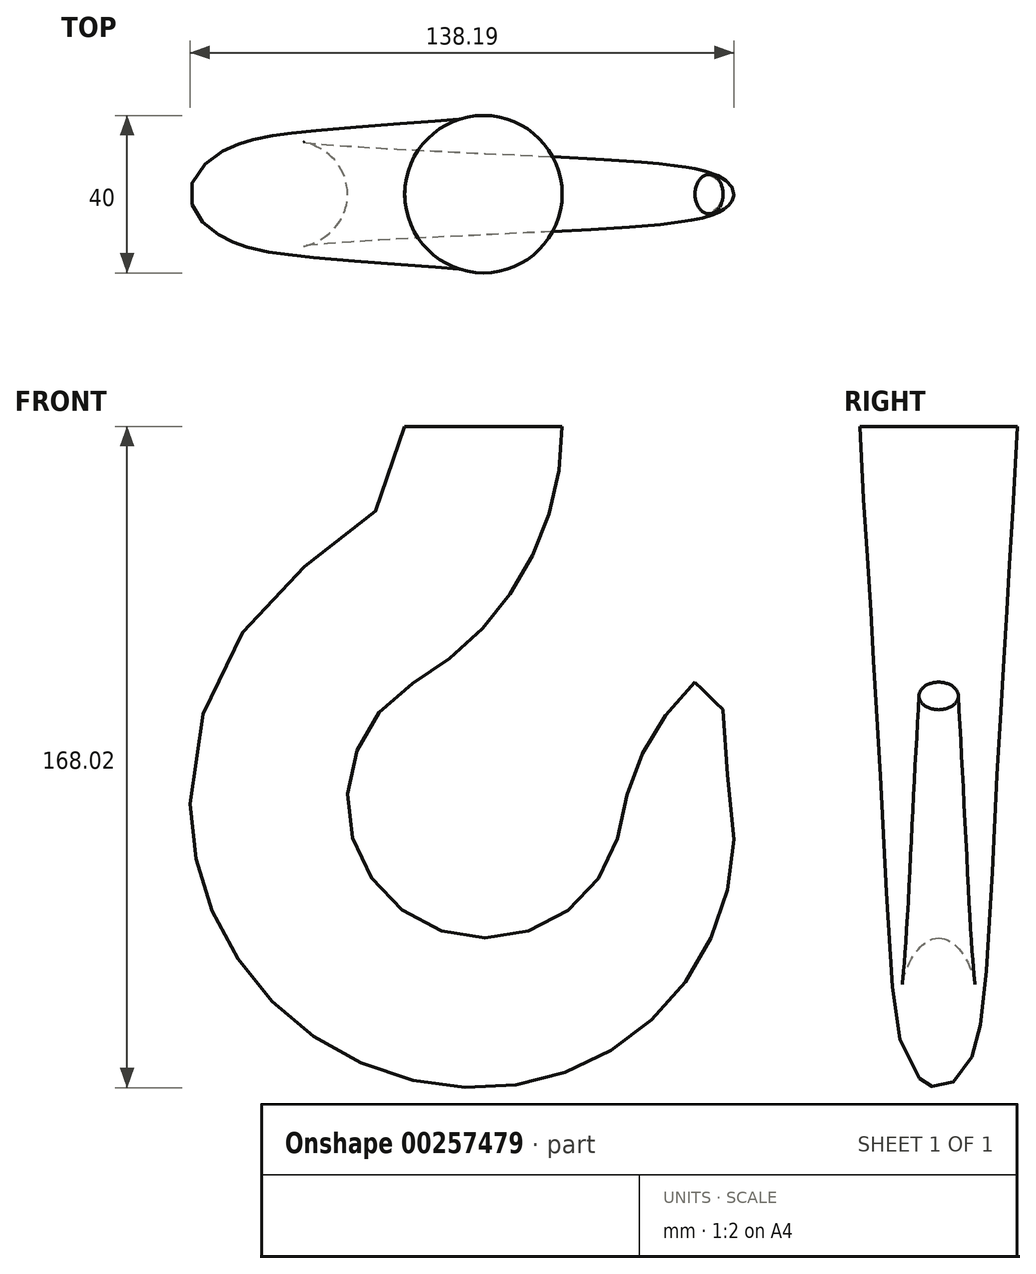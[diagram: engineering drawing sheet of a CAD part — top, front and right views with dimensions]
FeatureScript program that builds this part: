
annotation { "Feature Type Name" : "Feature", "Feature Type Description" : "" }
export const myFeature = defineFeature(function(context is Context, id is Id, definition is map)
    precondition{}
    {
        {
            var Q0;
            Q0=qCreatedBy(makeId("Front.planeOp"),FACE);
            var sketch = newSketch(context, id + "F0", { "sketchPlane" : qUnion([Q0])});
            skLineSegment(sketch, "E0", {"start": v(-20, 0) * mm, "end": v(20, 0) * mm, "construction": true});
            skArc(sketch, "E1", {"start": v(-37.36, -30.23) * mm, "mid": v(-24.65, -17.43) * mm, "end": v(-20, 0) * mm});
            skArc(sketch, "E2", {"start": v(-17.2, -64.77) * mm, "mid": v(10.04, -37.35) * mm, "end": v(20, 0) * mm});
            skLineSegment(sketch, "E3", {"start": v(-112.46, -95) * mm, "end": v(91.55, -95) * mm, "construction": true});
            skArc(sketch, "E4", {"start": v(-37.36, -30.23) * mm, "mid": v(-64.59, -57.65) * mm, "end": v(-74.55, -95) * mm});
            skArc(sketch, "E5", {"start": v(-74.55, -95) * mm, "mid": v(-52.62, -147.17) * mm, "end": v(0, -168) * mm});
            skArc(sketch, "E6", {"start": v(53.73, -65) * mm, "mid": v(41.39, -81) * mm, "end": v(35.06, -100.2) * mm});
            skLineSegment(sketch, "E7", {"start": v(53.73, -65) * mm, "end": v(60.87, -72) * mm, "construction": true});
            skArc(sketch, "E8", {"start": v(60.87, -72) * mm, "mid": v(60.74, -80.17) * mm, "end": v(61.94, -88.24) * mm});
            skCircle(sketch, "E9", {"center": v(57.3, -68.5) * mm, "radius": 5 * mm, "construction": true});
            skArc(sketch, "E10", {"start": v(0, -168) * mm, "mid": v(49.97, -142.88) * mm, "end": v(61.94, -88.24) * mm});
            skArc(sketch, "E11", {"start": v(-17.2, -64.77) * mm, "mid": v(-19.19, -123.97) * mm, "end": v(35.06, -100.2) * mm});
            skSolve(sketch);
        }
        {
            var Q0;
            Q0=qCreatedBy(makeId("Top.planeOp"),FACE);
            var sketch = newSketch(context, id + "F1", { "sketchPlane" : qUnion([Q0])});
            skLineSegment(sketch, "E12.0", {"start": v(-20, 0) * mm, "end": v(20, 0) * mm, "construction": true});
            skCircle(sketch, "E13", {"center": v(0, 0) * mm, "radius": 20 * mm});
            skSolve(sketch);
        }
        {
            var Q0;
            Q0=sQuery(id+"F0.wireOp",EDGE,"E7");
            cPlane(context, id + "F2", {"entities" : qUnion([Q0]), "cplaneType" : CPlaneType.LINE_ANGLE, "offset" : 25 * mm, "angle" : 90 * degree, "width" : 150 * mm, "height" : 150 * mm});
        }
        {
            var Q0;
            Q0=qCreatedBy(id+"F2.planeOp",FACE);
            var sketch = newSketch(context, id + "F3", { "sketchPlane" : qUnion([Q0])});
            skLineSegment(sketch, "E14.0", {"start": v(83.87, 0) * mm, "end": v(93.87, 0) * mm, "construction": true});
            skCircle(sketch, "E15", {"center": v(88.87, 0) * mm, "radius": 5 * mm});
            skSolve(sketch);
        }
        {
            var Q0;
            Q0=qCreatedBy(makeId("Front.planeOp"),FACE);
            var sketch = newSketch(context, id + "F4", { "sketchPlane" : qUnion([Q0])});
            skArc(sketch, "E16.0", {"start": v(-37.36, -30.23) * mm, "mid": v(-24.65, -17.43) * mm, "end": v(-20, 0) * mm});
            skArc(sketch, "E17.0", {"start": v(-37.36, -30.23) * mm, "mid": v(-64.59, -57.65) * mm, "end": v(-74.55, -95) * mm});
            skArc(sketch, "E18.0", {"start": v(-74.55, -95) * mm, "mid": v(-52.62, -147.17) * mm, "end": v(0, -168) * mm});
            skArc(sketch, "E19.0", {"start": v(60.87, -72) * mm, "mid": v(60.74, -80.17) * mm, "end": v(61.94, -88.24) * mm});
            skArc(sketch, "E20.0", {"start": v(0, -168) * mm, "mid": v(49.97, -142.88) * mm, "end": v(61.94, -88.24) * mm});
            skSolve(sketch);
        }
        {
            var Q0;
            Q0=qCreatedBy(makeId("Front.planeOp"),FACE);
            var sketch = newSketch(context, id + "F5", { "sketchPlane" : qUnion([Q0])});
            skArc(sketch, "E21.0", {"start": v(-17.2, -64.77) * mm, "mid": v(10.04, -37.35) * mm, "end": v(20, 0) * mm});
            skArc(sketch, "E22.0", {"start": v(-17.2, -64.77) * mm, "mid": v(-19.19, -123.97) * mm, "end": v(35.06, -100.2) * mm});
            skArc(sketch, "E23.0", {"start": v(53.73, -65) * mm, "mid": v(41.39, -81) * mm, "end": v(35.06, -100.2) * mm});
            skSolve(sketch);
        }
        {
            var Q0;
            Q0=makeQuery(id+"F3.imprint","IMPRINT",FACE,{"disambiguationData":[TD([[makeQuery(id+"F3.imprint","IMPRINT",EDGE,{"derivedFrom":sQuery(id+"F3.wireOp",EDGE,"E15")}),1.0]])]});
            var Q1;
            Q1=makeQuery(id+"F1.imprint","IMPRINT",FACE,{"disambiguationData":[TD([[makeQuery(id+"F1.imprint","IMPRINT",EDGE,{"derivedFrom":sQuery(id+"F1.wireOp",EDGE,"E13")}),1.0]])]});
            var Q2;
            Q2 = qConstructionFilter(qBodyType(qCreatedBy(id + "F5" ,EDGE), BodyType.WIRE), ConstructionObject.NO);
            var Q3;
            Q3 = qConstructionFilter(qBodyType(qCreatedBy(id + "F4" ,EDGE), BodyType.WIRE), ConstructionObject.NO);
            loft(context, id + "F6", {"addGuides" : true, "sheetProfilesArray" : [{ "sheetProfileEntities" : qUnion([Q0]) }, { "sheetProfileEntities" : qUnion([Q1]) }], "guidesArray" : [{ "guideEntities" : qUnion([Q2]), "guideDerivativeType" : LoftGuideDerivativeType.DEFAULT, "guideDerivativeMagnitude" : 1 }, { "guideEntities" : qUnion([Q3]), "guideDerivativeType" : LoftGuideDerivativeType.DEFAULT, "guideDerivativeMagnitude" : 1 }]});
        }
    });
